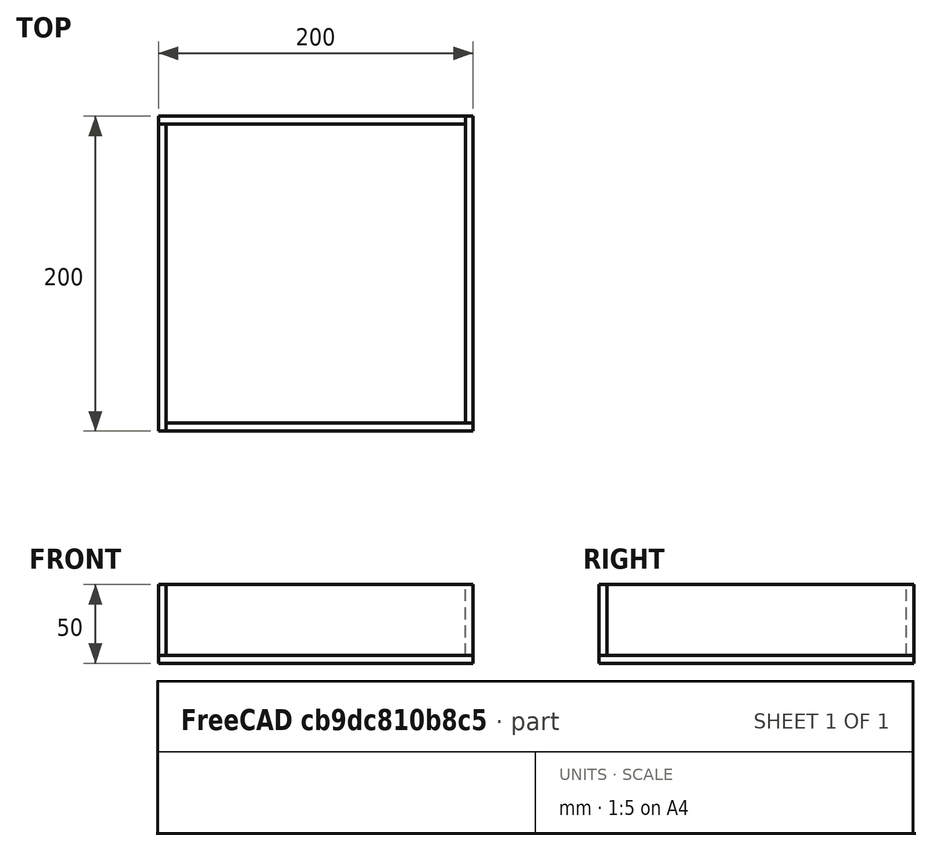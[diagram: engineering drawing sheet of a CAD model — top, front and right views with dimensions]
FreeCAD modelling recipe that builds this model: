
FCSTD DOCUMENT  (FreeCAD 0.19R24267 (Git))
Label: Ex005
License: Creative Commons Attribution
LicenseURL: http://creativecommons.org/licenses/by/4.0/
objects: TechDraw::DrawViewDimension×7, Part::Box×5, TechDraw::DrawViewSection×2, TechDraw::DrawSVGTemplate×1, App::DocumentObjectGroup×1, TechDraw::DrawProjGroupItem×1, TechDraw::DrawProjGroup×1, TechDraw::DrawViewPart×1, TechDraw::DrawPage×1
note: 5 computed .brp shape members not serialized (recipe doc carries the construction recipe); baked Part::Feature solids carry a one-line shape summary decoded from their .brp

FEATURE [Part::Box] Box  label="Cube"
  AttacherType = Attacher::AttachEngine3D
  Height = 5
  Length = 200
  Width = 200
FEATURE [Part::Box] Box001  label="Cube"
  AttacherType = Attacher::AttachEngine3D
  Height = 45
  Length = 195
  Placement = pos=(5,0,5) rot=(0,0,1;0rad)
  Width = 5
FEATURE [Part::Box] Box002  label="Cube"
  AttacherType = Attacher::AttachEngine3D
  Height = 45
  Length = 195
  Placement = pos=(5,-9e-16,5) rot=(0,0,1;1.5708rad)
  Width = 5
FEATURE [Part::Box] Box003  label="Cube"
  AttacherType = Attacher::AttachEngine3D
  Height = 45
  Length = 195
  Placement = pos=(4.4e-14,195,5) rot=(0,0,1;0rad)
  Width = 5
FEATURE [Part::Box] Box004  label="Cube"
  AttacherType = Attacher::AttachEngine3D
  Height = 45
  Length = 195
  Placement = pos=(195,200,5) rot=(0,0,1;4.71239rad)
  Width = 5
FEATURE [TechDraw::DrawSVGTemplate] Template
  EditableTexts = Designed_by_Name=JW; Drawing_number=01; FC-Date=04-04-2021; FC-SC=1:2; FC-SH=01; FC-Title=Ex005; Subtitle=twitch.tv/freecadfrance; Weight=NC
  Height = 210
  Orientation = 1
  Width = 297
FEATURE [App::DocumentObjectGroup] Groupe
  Group = -> [Box,Box001,Box002,Box003,Box004]
FEATURE [TechDraw::DrawProjGroupItem] ProjItem  label="Front"
  CoarseView = false
  Direction = (0,0,1)
  Focus = 100
  HardHidden = false
  IsoCount = 0
  IsoHidden = false
  IsoVisible = false
  LockPosition = true
  Perspective = false
  Rotation = 0
  RotationVector = (1,0,0)
  Scale = 0.5
  ScaleType = 2
  SeamHidden = false
  SeamVisible = true
  SmoothHidden = false
  SmoothVisible = true
  Source = -> [Groupe]
  Type = 0
  X = 0
  XDirection = (1,0,0)
  Y = 0
FEATURE [TechDraw::DrawProjGroup] ProjGroup
  Anchor = -> ProjItem
  AutoDistribute = true
  LockPosition = false
  ProjectionType = 0
  Rotation = 0
  Scale = 0.5
  ScaleType = 2
  Source = -> [Groupe]
  Views = -> [ProjItem]
  X = 80.4379
  Y = 103.659
  spacingX = 15
  spacingY = 15
FEATURE [TechDraw::DrawViewSection] SectionView  label="Section A - A"
  BaseView = -> ProjItem
  CoarseView = false
  CutSurfaceDisplay = 2
  Direction = (0,-1,0)
  FileGeomPattern = <path>
  FileHatchPattern = <path>
  Focus = 100
  FuseBeforeCut = false
  HardHidden = false
  HatchScale = 1
  IsoCount = 0
  IsoHidden = false
  IsoVisible = false
  LockPosition = false
  NameGeomPattern = Diamant
  Perspective = false
  Rotation = 0
  Scale = 0.5
  ScaleType = 0
  SeamHidden = false
  SeamVisible = true
  SectionDirection = 2
  SectionNormal = (0,-1,0)
  SectionOrigin = (100,100,25)
  SectionSymbol = A
  SmoothHidden = false
  SmoothVisible = true
  Source = -> [Groupe]
  X = 79.7809
  XDirection = (1,0,0)
  Y = 184.482
FEATURE [TechDraw::DrawViewSection] SectionView001  label="Section B - B"
  BaseView = -> ProjItem
  CoarseView = false
  CutSurfaceDisplay = 2
  Direction = (-1,0,0)
  FileGeomPattern = <path>
  FileHatchPattern = <path>
  Focus = 100
  FuseBeforeCut = false
  HardHidden = false
  HatchScale = 1
  IsoCount = 0
  IsoHidden = false
  IsoVisible = false
  LockPosition = false
  NameGeomPattern = Diamant
  Perspective = false
  Rotation = 0
  Scale = 0.5
  ScaleType = 0
  SeamHidden = false
  SeamVisible = true
  SectionDirection = 0
  SectionNormal = (-1,0,0)
  SectionOrigin = (100,100,25)
  SectionSymbol = B
  SmoothHidden = false
  SmoothVisible = true
  Source = -> [Groupe]
  X = 179
  XDirection = (0,0,1)
  Y = 124.032
FEATURE [TechDraw::DrawViewDimension] Dimension
  Arbitrary = false
  ArbitraryTolerances = false
  EqualTolerance = true
  FormatSpec = %.0f
  FormatSpecOverTolerance = %+.0f
  FormatSpecUnderTolerance = %+.0f
  Inverted = false
  LockPosition = false
  MeasureType = 1
  OverTolerance = 0
  References2D = -> [ProjItem]
  Rotation = 0
  ScaleType = 0
  TheoreticalExact = false
  Type = 1
  UnderTolerance = 0
  X = -22.2697
  Y = 59.1699
FEATURE [TechDraw::DrawViewDimension] Dimension001
  Arbitrary = false
  ArbitraryTolerances = false
  EqualTolerance = true
  FormatSpec = %.0f
  FormatSpecOverTolerance = %+.0f
  FormatSpecUnderTolerance = %+.0f
  Inverted = false
  LockPosition = false
  MeasureType = 1
  OverTolerance = 0
  References2D = -> [ProjItem]
  Rotation = 0
  ScaleType = 0
  TheoreticalExact = false
  Type = 1
  UnderTolerance = 0
  X = 12.9095
  Y = -59.3276
FEATURE [TechDraw::DrawViewDimension] Dimension002
  Arbitrary = false
  ArbitraryTolerances = false
  EqualTolerance = true
  FormatSpec = %.0f
  FormatSpecOverTolerance = %+.0f
  FormatSpecUnderTolerance = %+.0f
  Inverted = false
  LockPosition = false
  MeasureType = 1
  OverTolerance = 0
  References2D = -> [ProjItem]
  Rotation = 0
  ScaleType = 0
  TheoreticalExact = false
  Type = 1
  UnderTolerance = 0
  X = -1.61439
  Y = -70.8077
FEATURE [TechDraw::DrawViewDimension] Dimension003
  Arbitrary = false
  ArbitraryTolerances = false
  EqualTolerance = true
  FormatSpec = %.0f
  FormatSpecOverTolerance = %+.0f
  FormatSpecUnderTolerance = %+.0f
  Inverted = false
  LockPosition = false
  MeasureType = 1
  OverTolerance = 0
  References2D = -> [ProjItem]
  Rotation = 0
  ScaleType = 0
  TheoreticalExact = false
  Type = 1
  UnderTolerance = 0
  X = -62.6517
  Y = -54.1855
FEATURE [TechDraw::DrawViewDimension] Dimension004
  Arbitrary = false
  ArbitraryTolerances = false
  EqualTolerance = true
  FormatSpec = %.0f
  FormatSpecOverTolerance = %+.0f
  FormatSpecUnderTolerance = %+.0f
  Inverted = false
  LockPosition = false
  MeasureType = 1
  OverTolerance = 0
  References2D = -> [SectionView001]
  Rotation = 0
  ScaleType = 0
  TheoreticalExact = false
  Type = 1
  UnderTolerance = 0
  X = -25.0562
  Y = 57.9931
FEATURE [TechDraw::DrawViewDimension] Dimension005
  Arbitrary = false
  ArbitraryTolerances = false
  EqualTolerance = true
  FormatSpec = %.0f
  FormatSpecOverTolerance = %+.0f
  FormatSpecUnderTolerance = %+.0f
  Inverted = false
  LockPosition = false
  MeasureType = 1
  OverTolerance = 0
  References2D = -> [SectionView001]
  Rotation = 0
  ScaleType = 0
  TheoreticalExact = false
  Type = 1
  UnderTolerance = 0
  X = -3.31746
  Y = 57.9931
FEATURE [TechDraw::DrawViewDimension] Dimension006
  Arbitrary = false
  ArbitraryTolerances = false
  EqualTolerance = true
  FormatSpec = %.0f
  FormatSpecOverTolerance = %+.0f
  FormatSpecUnderTolerance = %+.0f
  Inverted = false
  LockPosition = false
  MeasureType = 1
  OverTolerance = 0
  References2D = -> [SectionView001]
  Rotation = 0
  ScaleType = 0
  TheoreticalExact = false
  Type = 1
  UnderTolerance = 0
  X = -3.94463
  Y = 65.1557
FEATURE [TechDraw::DrawViewPart] View
  CoarseView = false
  Direction = (0.577,-0.577,0.577)
  Focus = 100
  HardHidden = false
  IsoCount = 0
  IsoHidden = false
  IsoVisible = false
  LockPosition = false
  Perspective = false
  Rotation = 0
  Scale = 0.2
  ScaleType = 0
  SeamHidden = false
  SeamVisible = true
  SmoothHidden = false
  SmoothVisible = true
  Source = -> [Groupe]
  X = 245.952
  XDirection = (0.707,0.707,0)
  Y = 89.0059
FEATURE [TechDraw::DrawPage] Page
  KeepUpdated = true
  NextBalloonIndex = 1
  ProjectionType = 0
  Template = -> Template
  Views = -> [ProjGroup,SectionView,SectionView001,Dimension,Dimension001,Dimension002,Dimension003,Dimension004,Dimension005,Dimension006,View]
note: 4 file-system paths scrubbed to <path> (originals preserved in the JSON sidecar)
